# Revit family: WashBasin-98cm-Vitra_SentoSeries_5948
name_source: partatom
category: Plumbing Fixtures
revit_build: Autodesk Revit 2017 (Build: 20160225_1515(x64)
units: mm (PartAtom-declared; Revit-internal decimal feet)

## family parameters
Cut with Voids When Loaded = No
Host = Face
OmniClass Number = 23.45.05.14.14
OmniClass Title = Sinks/Lavatories
Part Type = Normal
Room Calculation Point = No
Round Connector Dimension = Use Diameter
Shared = Yes

## types (1)
- WashBasin-Vanity Washbasin-98cm-Vitra_SentoSeries_5948B003-0001
    Article No. (default) = 5948B003-0001
    BIMobject category = Sanitary - Basins
    Brand = VitrA
    CW Connection = No
    Color = White
    Default Elevation = 850 mm  [stored 2.78871 ft]
    Description = Sento Vanity Washbasin 
With Tap Hole - With Overflow Hole - 98cm - White
    Design country = Turkey
    HW Connection = No
    IFC Classification = Sanitary Terminal
    Main Material = Ceramic
    Manufacturer = VitrA
    Manufacturer name = Vitra
    Masterformat 2014 Code = 22 41 16
    Masterformat 2014 Description = Residential Lavatories and Sinks
    Model = 5948B003-0001
    Mounting type = Wall-Hung
    NBS Referans Code = 35-65-70-94
    NBS Referans Description = Wash Basin Systems
    Nominal Depth (mm) = 485 mm  [stored 1.59121 ft]
    Nominal Height (mm) = 190 mm
    Nominal Width (mm) = 980 mm  [stored 3.21522 ft]
    OmniClass Code = 23.45.05.14.14
    OmniClass Description = Sinks/Lavatories
    Primary Material = Matte White
    Product SKU = 5948B003-0001
    Product certification = https://www.vitraglobal.com
    Product data url = https://www.bimobject.com
    Product family = Sento
    Product group = Vanity Washbasin
    Product url = https://www.vitra-bad.de
    Technical description = https://cdn.vitra.com.tr
    UNSPSC Code = 301815
    URL = https://vitraglobal.com
    Uniclass 1.4 Code = L7212
    Uniclass 1.4 Description = Washbasins
    Uniclass 2.0 Code = SS-35-65-70-94
    Uniclass 2.0 Description = Sanitary Dispensing And Disposal Units
    Uniclass 2015 Code = Pr_40_20_96_81
    Uniclass 2015 Name = Wash basins, Sinks and troughs
    Uniformat II Code = D2010
    Uniformat II Description = Plumbing Fixtures
    Vent Connection = No
    Warranty Period (Year) = 10 Years
    Waste Connection = Yes
    Weight Net (kg) = 29.3
    Youtube = https://www.youtube.com

note: [stored X ft] marks values corroborated as IEEE doubles in the binary element streams (Revit-internal decimal feet)

## geometry (parser evidence)
native form markers: Sweep x3
no freeform markers — native parametric forms only
